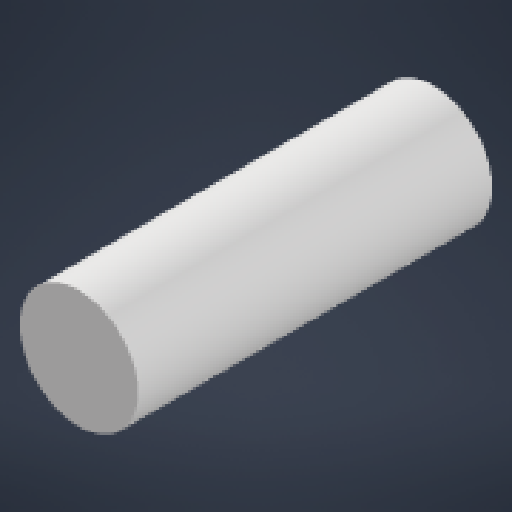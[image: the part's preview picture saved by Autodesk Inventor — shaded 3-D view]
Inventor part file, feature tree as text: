
AUTODESK INVENTOR PART (.ipt)
format: ipt  version: 2024 (Build 280153000, 153)  size: 133,120 bytes
history: native  units: mm
features: extrude x2, other x1, sketch x1
ambient origin geometry x8: Origin, YZ Plane, XZ Plane, XY Plane, X Axis, Y Axis, Z Axis, Center Point
bodies: Body1 (feature_tree)
feature tree (4):
  other  "솔리드1"
  sketch  "스케치1"
  extrude  "돌출1"  Depth=10.0mm
  extrude  "돌출2"  Depth=5.0mm
